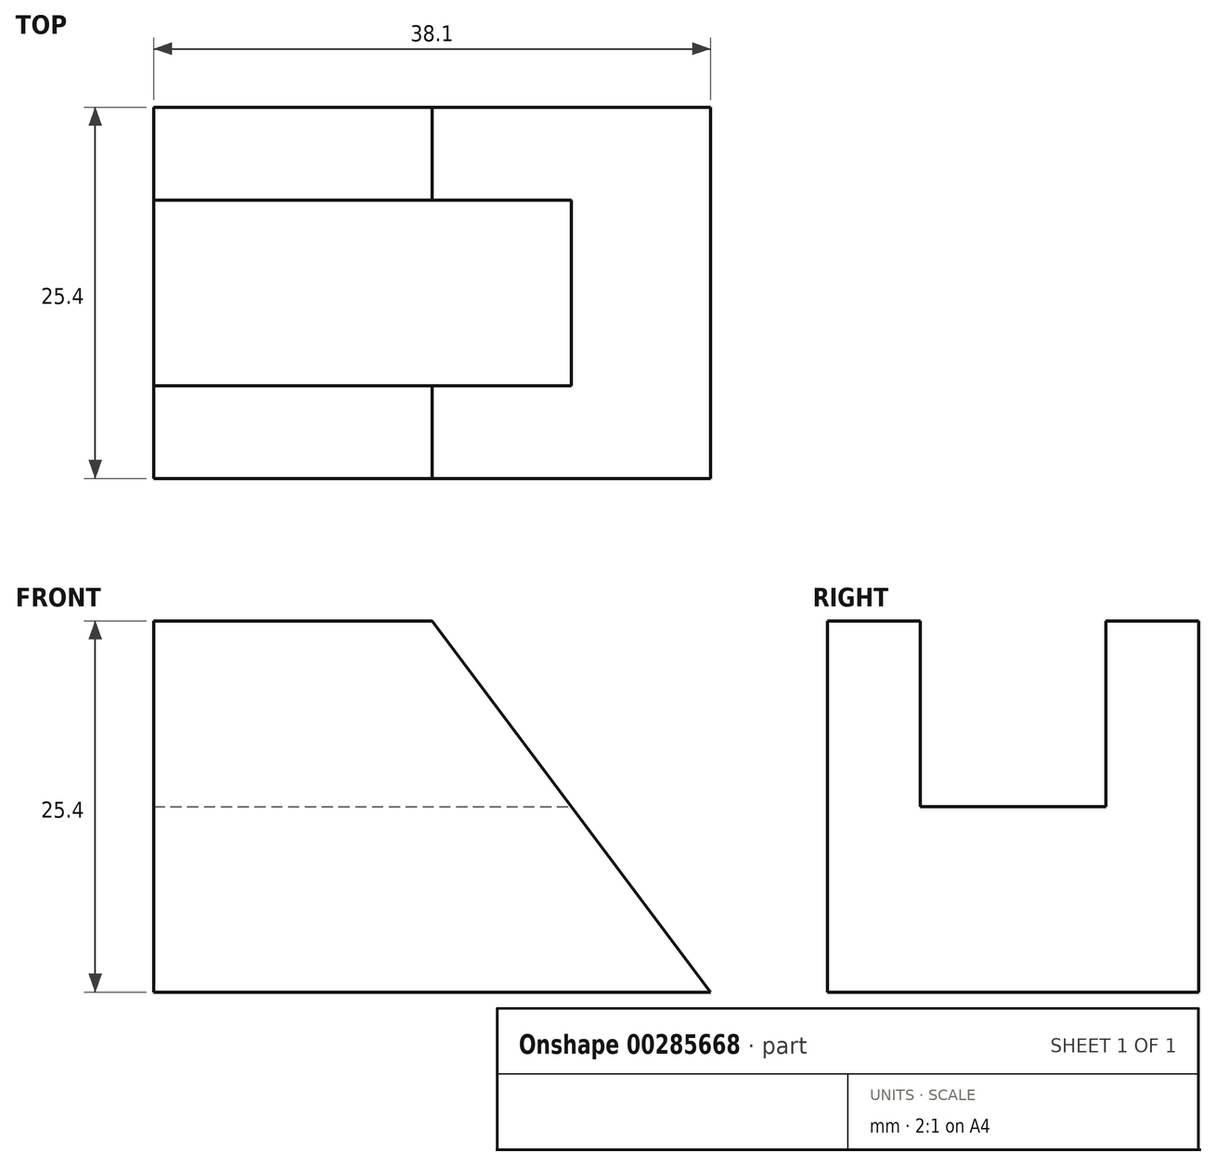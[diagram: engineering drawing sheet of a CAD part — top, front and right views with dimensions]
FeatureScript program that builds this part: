
annotation { "Feature Type Name" : "Feature", "Feature Type Description" : "" }
export const myFeature = defineFeature(function(context is Context, id is Id, definition is map)
    precondition{}
    {
        {
            var Q0;
            Q0=qCreatedBy(makeId("Front.planeOp"),FACE);
            var sketch = newSketch(context, id + "F0", { "sketchPlane" : qUnion([Q0])});
            skLineSegment(sketch, "E0", {"start": v(0, 0) * mm, "end": v(0, 25.4) * mm});
            skLineSegment(sketch, "E1", {"start": v(0, 25.4) * mm, "end": v(19.05, 25.4) * mm});
            skLineSegment(sketch, "E2", {"start": v(19.05, 25.4) * mm, "end": v(38.1, 0) * mm});
            skLineSegment(sketch, "E3", {"start": v(38.1, 0) * mm, "end": v(0, 0) * mm});
            skSolve(sketch);
        }
        {
            var Q0;
            Q0 = qSketchRegion(id + "F0", true);
            extrude(context, id + "F1", {"entities" : qUnion([Q0]), "depth" : 6.35 * mm});
        }
        {
            var Q0;
            Q0=makeQuery(id+"F1.opExtrude","CAP_FACE",FACE,{"disambiguationData":[OSD([sQuery(id+"F0.wireOp",EDGE,"E0"),sQuery(id+"F0.wireOp",EDGE,"E1"),sQuery(id+"F0.wireOp",EDGE,"E2"),sQuery(id+"F0.wireOp",EDGE,"E3")])],"isStart":false});
            var sketch = newSketch(context, id + "F2", { "sketchPlane" : qUnion([Q0])});
            skLineSegment(sketch, "E4", {"start": v(0, 0) * mm, "end": v(0, 12.7) * mm});
            skLineSegment(sketch, "E5", {"start": v(0, 12.7) * mm, "end": v(28.58, 12.7) * mm});
            skLineSegment(sketch, "E6", {"start": v(28.58, 12.7) * mm, "end": v(38.1, 0) * mm});
            skLineSegment(sketch, "E7", {"start": v(38.1, 0) * mm, "end": v(0, 0) * mm});
            skSolve(sketch);
        }
        {
            var Q0;
            Q0 = qSketchRegion(id + "F2", true);
            extrude(context, id + "F3", {"entities" : qUnion([Q0]), "operationType" : NewBodyOperationType.ADD, "depth" : 12.7 * mm});
        }
        {
            var Q0;
            Q0=makeQuery(id+"F3.opExtrude","CAP_FACE",FACE,{"disambiguationData":[OSD([sQuery(id+"F2.wireOp",EDGE,"E4"),sQuery(id+"F2.wireOp",EDGE,"E5"),sQuery(id+"F2.wireOp",EDGE,"E6"),sQuery(id+"F2.wireOp",EDGE,"E7")])],"isStart":false});
            var sketch = newSketch(context, id + "F4", { "sketchPlane" : qUnion([Q0])});
            skLineSegment(sketch, "E8", {"start": v(0, 25.4) * mm, "end": v(0, 0) * mm});
            skLineSegment(sketch, "E9", {"start": v(0, 0) * mm, "end": v(38.1, 0) * mm});
            skLineSegment(sketch, "E10", {"start": v(38.1, 0) * mm, "end": v(19.05, 25.4) * mm});
            skLineSegment(sketch, "E11", {"start": v(19.05, 25.4) * mm, "end": v(0, 25.4) * mm});
            skSolve(sketch);
        }
        {
            var Q0;
            Q0 = qSketchRegion(id + "F4", true);
            extrude(context, id + "F5", {"entities" : qUnion([Q0]), "operationType" : NewBodyOperationType.ADD, "depth" : 6.35 * mm});
        }
    });
